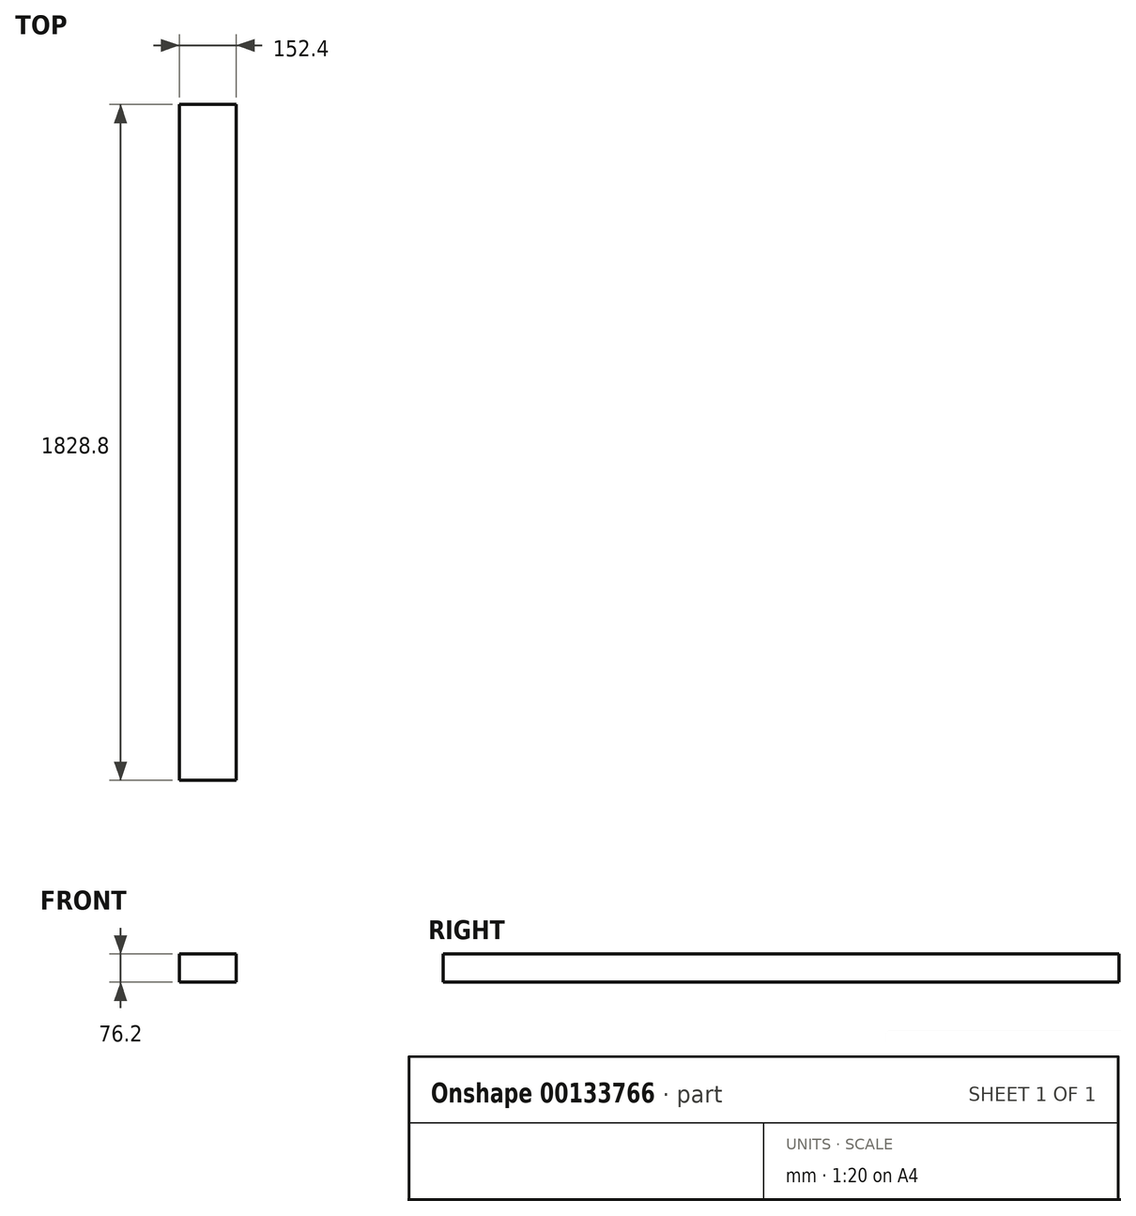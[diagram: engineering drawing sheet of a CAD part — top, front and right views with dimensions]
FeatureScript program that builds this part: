
annotation { "Feature Type Name" : "Feature", "Feature Type Description" : "" }
export const myFeature = defineFeature(function(context is Context, id is Id, definition is map)
    precondition{}
    {
        {
            var Q0;
            Q0=qCreatedBy(makeId("Front.planeOp"),FACE);
            var sketch = newSketch(context, id + "F0", { "sketchPlane" : qUnion([Q0])});
            skLineSegment(sketch, "E0.bottom", {"start": v(-35.06, 83.17) * mm, "end": v(117.34, 83.17) * mm});
            skLineSegment(sketch, "E0.top", {"start": v(-35.06, 6.97) * mm, "end": v(117.34, 6.97) * mm});
            skLineSegment(sketch, "E0.left", {"start": v(-35.06, 83.17) * mm, "end": v(-35.06, 6.97) * mm});
            skLineSegment(sketch, "E0.right", {"start": v(117.34, 83.17) * mm, "end": v(117.34, 6.97) * mm});
            skSolve(sketch);
        }
        {
            var Q0;
            Q0=makeQuery(id+"F0.imprint","IMPRINT",FACE,{"disambiguationData":[TD([[makeQuery(id+"F0.imprint","IMPRINT",EDGE,{"derivedFrom":sQuery(id+"F0.wireOp",EDGE,"E0.bottom")}),-1.0]])]});
            extrude(context, id + "F1", {"entities" : qUnion([Q0]), "depth" : 1828.8 * mm});
        }
    });
